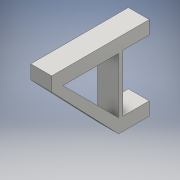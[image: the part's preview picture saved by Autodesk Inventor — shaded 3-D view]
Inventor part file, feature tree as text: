
AUTODESK INVENTOR PART (.ipt)
format: ipt  version: 2016 (Build 200138000, 138)  size: 125,952 bytes
history: native  units: mm
features: extrude x4, sketch x4
ambient origin geometry x8: Origin, YZ Plane, XZ Plane, XY Plane, X Axis, Y Axis, Z Axis, Center Point
bodies: Solid1 (feature_tree)
feature tree (8):
  extrude  "Extrusion1"  Depth=60.0mm
  extrude  "Extrusion2"  Depth=41.0mm
  extrude  "Extrusion3"  Depth=10.0mm
  extrude  "Extrusion4"  Depth=15.0mm TaperAngle=0.0deg
  sketch  "Sketch1"  dims[d0=15.0mm d1=60.0mm]
  sketch  "Sketch2"  dims[d2=3.0mm d3=0.0mm d4=41.0mm]
  sketch  "Sketch3"  dims[d5=19.0mm d6=0.0mm d7=10.0mm]
  sketch  "Sketch4"  dims[d8=48.0mm d9=15.0mm d10=0.0mm d11=10.0mm d12=45.0deg d13=15.0mm d14=0.0mm]
